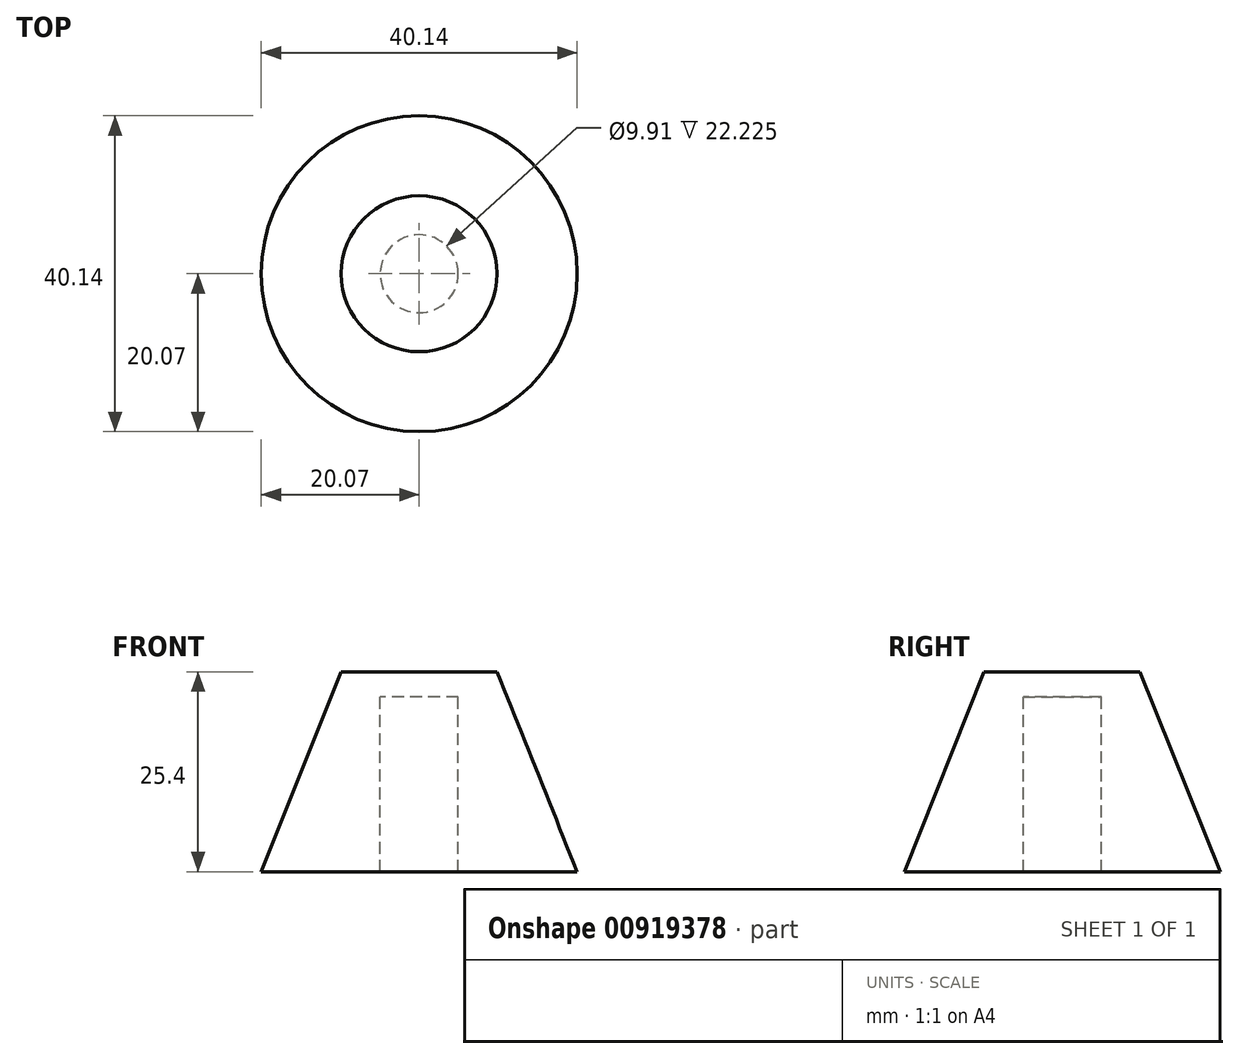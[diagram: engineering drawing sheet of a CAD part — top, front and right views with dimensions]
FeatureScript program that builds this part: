
annotation { "Feature Type Name" : "Feature", "Feature Type Description" : "" }
export const myFeature = defineFeature(function(context is Context, id is Id, definition is map)
    precondition{}
    {
        {
            var Q0;
            Q0=qCreatedBy(makeId("Front.planeOp"),FACE);
            var sketch = newSketch(context, id + "F0", { "sketchPlane" : qUnion([Q0])});
            skLineSegment(sketch, "E0", {"start": v(0, 0) * mm, "end": v(4.95, 0) * mm});
            skLineSegment(sketch, "E1", {"start": v(0, 0) * mm, "end": v(9.9, 0) * mm});
            skLineSegment(sketch, "E2", {"start": v(4.95, 0) * mm, "end": v(4.95, 25.4) * mm});
            skLineSegment(sketch, "E3", {"start": v(4.95, 25.4) * mm, "end": v(0, 25.4) * mm});
            skLineSegment(sketch, "E4", {"start": v(0, 25.4) * mm, "end": v(0, 0) * mm});
            skLineSegment(sketch, "E5", {"start": v(9.9, 25.4) * mm, "end": v(4.95, 25.4) * mm});
            skLineSegment(sketch, "E6", {"start": v(9.9, 25.4) * mm, "end": v(9.9, 0) * mm});
            skLineSegment(sketch, "E7", {"start": v(9.9, 25.4) * mm, "end": v(20.07, 0) * mm});
            skLineSegment(sketch, "E8", {"start": v(20.07, 0) * mm, "end": v(9.9, 0) * mm});
            skLineSegment(sketch, "E9", {"start": v(0, 25.4) * mm, "end": v(0, 22.23) * mm});
            skLineSegment(sketch, "E10", {"start": v(0, 22.23) * mm, "end": v(4.95, 22.23) * mm});
            skSolve(sketch);
        }
        {
            var Q0;
            {var subQ2=sQuery(id+"F0.wireOp",EDGE,"E2");Q0=makeQuery(id+"F0.imprint","IMPRINT",FACE,{"disambiguationData":[TD([[makeQuery(id+"F0.imprint","IMPRINT",EDGE,{"derivedFrom":subQ2}),-1.0]])]});}
            var Q1;
            Q1=makeQuery(id+"F0.imprint","IMPRINT",FACE,{"disambiguationData":[TD([[makeQuery(id+"F0.imprint","IMPRINT",EDGE,{"derivedFrom":sQuery(id+"F0.wireOp",EDGE,"E6")}),1.0]])]});
            var Q2;
            {var subQ0=sQuery(id+"F0.wireOp",EDGE,"E3");Q2=makeQuery(id+"F0.imprint","IMPRINT",FACE,{"disambiguationData":[TD([[makeQuery(id+"F0.imprint","IMPRINT",EDGE,{"derivedFrom":subQ0}),1.0]])]});}
            var Q3;
            Q3=sQuery(id+"F0.wireOp",EDGE,"E4");
            revolve(context, id + "F1", {"surfaceOperationType" : NewSurfaceOperationType.NEW, "entities" : qUnion([Q0, Q1, Q2]), "axis" : qUnion([Q3]), "revolveType" : RevolveType.FULL});
        }
    });
